# Revit family: Faucet-Lavatory-KOHLER-KUMIN-K-99448T
name_source: partatom
category: Plumbing Fixtures
units: mm (PartAtom-declared; Revit-internal decimal feet)

## family parameters
Cut with Voids When Loaded = No
Host = Face
Maintain Annotation Orientation = No
OmniClass Number = 23.31.11.00
Part Type = Normal
Room Calculation Point = No
Round Connector Dimension = Use Diameter
Shared = No

## types (4) — shared parameters
ADA Compliant = No
Assembly Code = D2010
CW Connection = Yes
Cold Water Inlet = Cold Water Inlet
Date Modified = 01/12/2025
Default Elevation = 36"
Handle Clearance = 3 3/16"
Height = 13 3/8"
Hot Water Inlet = Hot Water Inlet
Length = 4 3/4"
Manufacturer = Kohler Co.
Master Format 2014 = 22 41 39
Master Format 2014 Name = Residential Faucets, Supplies, and Trim
Material = Premium Metal Construction
Product Name = KUMIN
Spout Reach = 4 3/4"
URL = http://www.kohler.com.cn
Vent Connection = No
Waste Connection = No
Waste Water Outlet = Waste Water Outlet
WaterSense Certified = No
Width = 1 7/8"

## per-type parameters (varying)
| type | Description | Dist1 | Drain Included | Finish | Flow Rate | HW Connection | Hot Water Connector Dia | Model | Pressure | Product Documentation Link | Product Page URL | Type | W/O Drain |
| 1.2 GPM, CP-Polished Chrome | Single Lever Tall Lavatory Faucet | 1 1/2" | No | Kohler-Metal-CP-Polished_Chrome | 1 GPM | Yes | 1/2" | K-99448T-4E2-CP | 60.00 psi |  |  | 1 | Yes |
| Cold Only, 1.5GPM, CP-Polished Chrome | E50 Cold Water Tall Lavatory Faucet | 0" | Yes | Kohler-Metal-CP-Polished_Chrome | 2 GPM | No | 0" | K-99448T-4CDE-CP | 45.00 psi |  |  | 4 | No |
| 1.2 GPM, BL-Matte Black | Single Lever Tall Lavatory Faucet | 1 1/2" | No | Kohler-Metal-BL-Matte_Black | 1 GPM | Yes | 1/2" | K-99448T-4E2-CP | 60.00 psi |  |  | 1 | Yes |
| 2.2 GPM, CP-Polished Chrome | single-handle bowl faucet | 1 1/2" | No | Kohler-Metal-CP-Polished_Chrome | 2 GPM | Yes | 1/2" | K-99448T-4-CP | 60.00 psi | https://files.kohler.com.cn | https://www.kohler.com.cn | 3 | Yes |

## geometry (parser evidence)
native form markers: Sweep x7
no freeform markers — native parametric forms only
